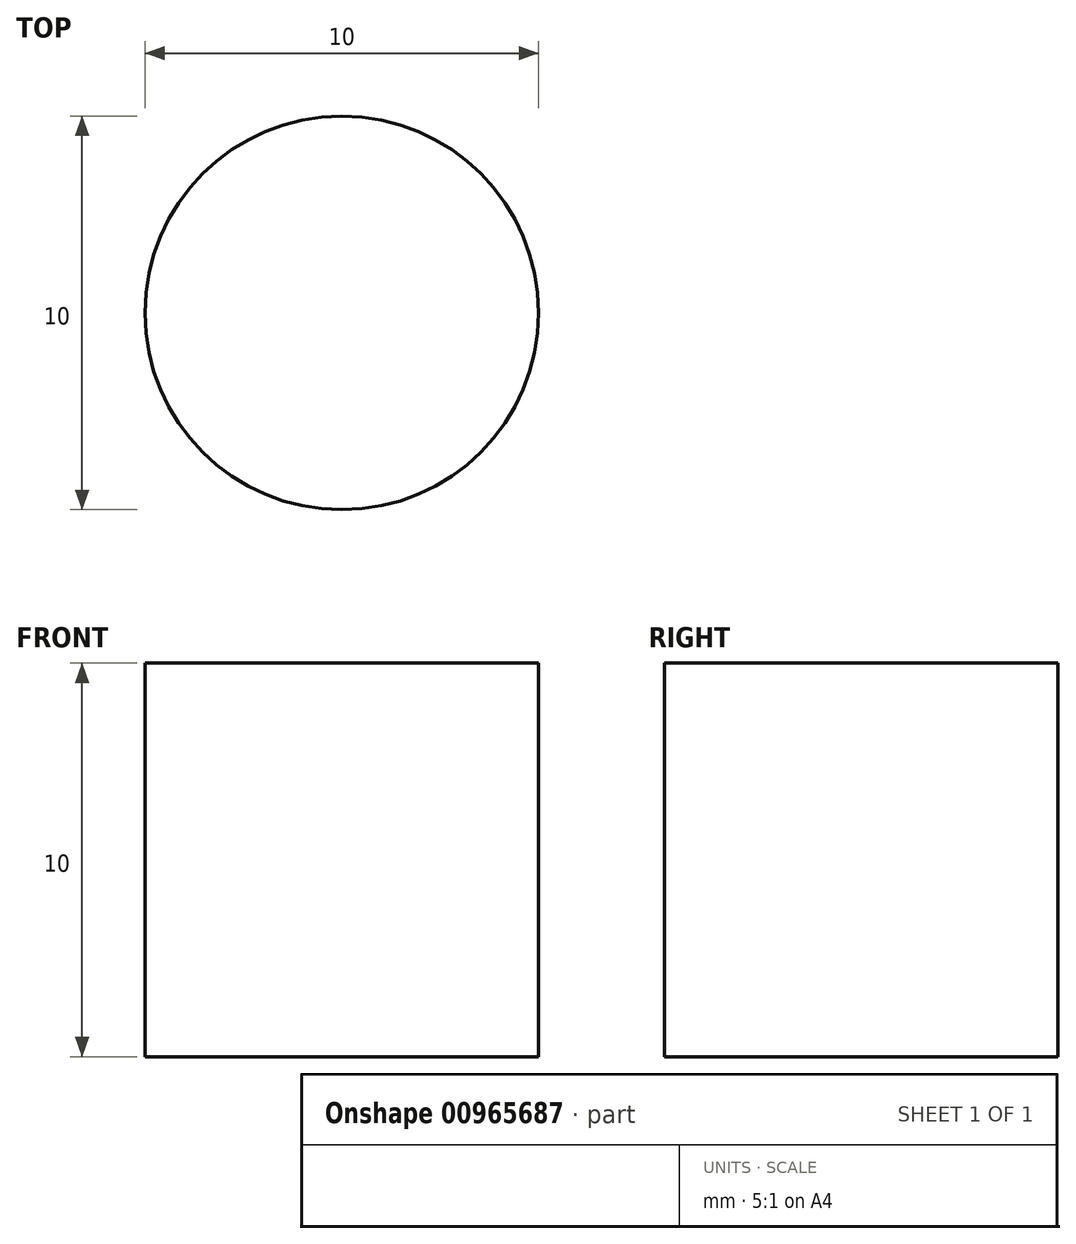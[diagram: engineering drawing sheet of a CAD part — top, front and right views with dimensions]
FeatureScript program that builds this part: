
annotation { "Feature Type Name" : "Feature", "Feature Type Description" : "" }
export const myFeature = defineFeature(function(context is Context, id is Id, definition is map)
    precondition{}
    {
        {
            var Q0;
            Q0=qCreatedBy(makeId("Top.planeOp"),FACE);
            var sketch = newSketch(context, id + "F0", { "sketchPlane" : qUnion([Q0])});
            skCircle(sketch, "E0", {"center": v(0, 1.5) * mm, "radius": 5 * mm});
            skSolve(sketch);
        }
        {
            var Q0;
            Q0=sQuery(id+"F0.wireOp",EDGE,"E0");
            extrude(context, id + "F1", {"bodyType" : ToolBodyType.SURFACE, "surfaceEntities" : qUnion([Q0]), "depth" : 10 * mm, "offsetDistance" : 25 * mm});
        }
    });
